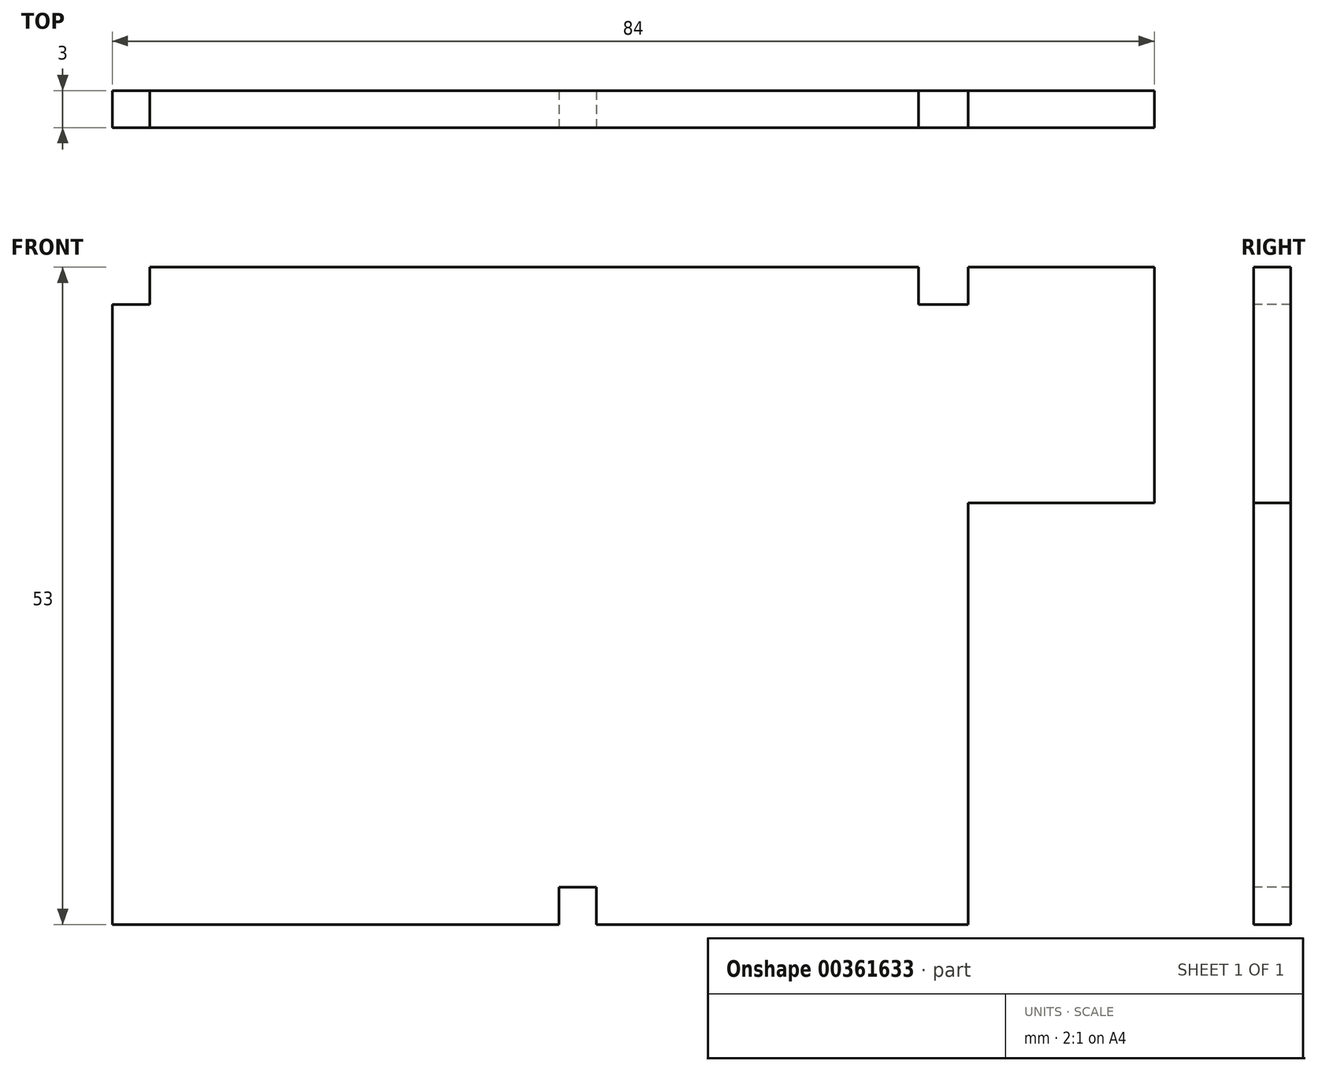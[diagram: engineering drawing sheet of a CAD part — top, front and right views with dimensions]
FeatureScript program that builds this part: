
annotation { "Feature Type Name" : "Feature", "Feature Type Description" : "" }
export const myFeature = defineFeature(function(context is Context, id is Id, definition is map)
    precondition{}
    {
        {
            var Q0;
            Q0=qCreatedBy(makeId("Front.planeOp"),FACE);
            var sketch = newSketch(context, id + "F0", { "sketchPlane" : qUnion([Q0])});
            skLineSegment(sketch, "E0.bottom", {"start": v(-24.73, 20.13) * mm, "end": v(59.27, 20.13) * mm});
            skLineSegment(sketch, "E0.top", {"start": v(-24.73, -32.87) * mm, "end": v(59.27, -32.87) * mm});
            skLineSegment(sketch, "E0.left", {"start": v(-24.73, 20.13) * mm, "end": v(-24.73, -32.87) * mm});
            skLineSegment(sketch, "E0.right", {"start": v(59.27, 20.13) * mm, "end": v(59.27, -32.87) * mm});
            skSolve(sketch);
        }
        {
            var Q0;
            Q0 = qSketchRegion(id + "F0", true);
            extrude(context, id + "F1", {"entities" : qUnion([Q0]), "depth" : 3 * mm});
        }
        {
            var Q0;
            Q0=makeQuery(id+"F1.opExtrude","CAP_FACE",FACE,{"disambiguationData":[OSD([sQuery(id+"F0.wireOp",EDGE,"E0.bottom"),sQuery(id+"F0.wireOp",EDGE,"E0.top"),sQuery(id+"F0.wireOp",EDGE,"E0.left"),sQuery(id+"F0.wireOp",EDGE,"E0.right")])],"isStart":false});
            var sketch = newSketch(context, id + "F2", { "sketchPlane" : qUnion([Q0])});
            skLineSegment(sketch, "E1.bottom", {"start": v(59.27, -32.87) * mm, "end": v(44.27, -32.87) * mm});
            skLineSegment(sketch, "E1.top", {"start": v(59.27, 1.13) * mm, "end": v(44.27, 1.13) * mm});
            skLineSegment(sketch, "E1.left", {"start": v(59.27, -32.87) * mm, "end": v(59.27, 1.13) * mm});
            skLineSegment(sketch, "E1.right", {"start": v(44.27, -32.87) * mm, "end": v(44.27, 1.13) * mm});
            skSolve(sketch);
        }
        {
            var Q0;
            Q0 = qSketchRegion(id + "F2", true);
            extrude(context, id + "F3", {"entities" : qUnion([Q0]), "operationType" : NewBodyOperationType.REMOVE, "oppositeDirection" : true, "depth" : 25 * mm});
        }
        {
            var Q0;
            Q0=makeQuery(id+"F1.opExtrude","CAP_FACE",FACE,{"disambiguationData":[OSD([sQuery(id+"F0.wireOp",EDGE,"E0.bottom"),sQuery(id+"F0.wireOp",EDGE,"E0.top"),sQuery(id+"F0.wireOp",EDGE,"E0.left"),sQuery(id+"F0.wireOp",EDGE,"E0.right")])],"isStart":false});
            var sketch = newSketch(context, id + "F4", { "sketchPlane" : qUnion([Q0])});
            skLineSegment(sketch, "E2", {"start": v(59.27, 20.13) * mm, "end": v(44.27, 20.13) * mm});
            skLineSegment(sketch, "E3", {"start": v(44.27, 20.13) * mm, "end": v(44.27, 17.13) * mm});
            skLineSegment(sketch, "E4", {"start": v(44.27, 17.13) * mm, "end": v(40.27, 17.13) * mm});
            skLineSegment(sketch, "E5", {"start": v(40.27, 17.13) * mm, "end": v(40.27, 20.13) * mm});
            skLineSegment(sketch, "E6", {"start": v(40.27, 20.13) * mm, "end": v(44.27, 20.13) * mm});
            skSolve(sketch);
        }
        {
            var Q0;
            Q0 = qSketchRegion(id + "F4", true);
            extrude(context, id + "F5", {"entities" : qUnion([Q0]), "operationType" : NewBodyOperationType.REMOVE, "oppositeDirection" : true, "depth" : 25 * mm});
        }
        {
            var Q0;
            Q0=makeQuery(id+"F1.opExtrude","CAP_FACE",FACE,{"disambiguationData":[OSD([sQuery(id+"F0.wireOp",EDGE,"E0.bottom"),sQuery(id+"F0.wireOp",EDGE,"E0.top"),sQuery(id+"F0.wireOp",EDGE,"E0.left"),sQuery(id+"F0.wireOp",EDGE,"E0.right")])],"isStart":false});
            var sketch = newSketch(context, id + "F6", { "sketchPlane" : qUnion([Q0])});
            skLineSegment(sketch, "E7", {"start": v(-24.73, 20.13) * mm, "end": v(-21.73, 20.13) * mm});
            skLineSegment(sketch, "E8", {"start": v(-21.73, 20.13) * mm, "end": v(-21.73, 17.13) * mm});
            skLineSegment(sketch, "E9", {"start": v(-21.73, 17.13) * mm, "end": v(-24.73, 17.13) * mm});
            skLineSegment(sketch, "E10", {"start": v(-24.73, 17.13) * mm, "end": v(-24.73, 20.13) * mm});
            skSolve(sketch);
        }
        {
            var Q0;
            Q0 = qSketchRegion(id + "F6", true);
            extrude(context, id + "F7", {"entities" : qUnion([Q0]), "operationType" : NewBodyOperationType.REMOVE, "oppositeDirection" : true, "depth" : 25 * mm});
        }
        {
            var Q0;
            Q0=makeQuery(id+"F1.opExtrude","CAP_FACE",FACE,{"disambiguationData":[OSD([sQuery(id+"F0.wireOp",EDGE,"E0.bottom"),sQuery(id+"F0.wireOp",EDGE,"E0.top"),sQuery(id+"F0.wireOp",EDGE,"E0.left"),sQuery(id+"F0.wireOp",EDGE,"E0.right")])],"isStart":false});
            var sketch = newSketch(context, id + "F8", { "sketchPlane" : qUnion([Q0])});
            skLineSegment(sketch, "E11", {"start": v(44.27, -32.87) * mm, "end": v(14.27, -32.87) * mm});
            skLineSegment(sketch, "E12", {"start": v(14.27, -32.87) * mm, "end": v(14.27, -29.87) * mm});
            skLineSegment(sketch, "E13", {"start": v(14.27, -29.87) * mm, "end": v(11.27, -29.87) * mm});
            skLineSegment(sketch, "E14", {"start": v(11.27, -29.87) * mm, "end": v(11.27, -32.87) * mm});
            skLineSegment(sketch, "E15", {"start": v(11.27, -32.87) * mm, "end": v(14.27, -32.87) * mm});
            skSolve(sketch);
        }
        {
            var Q0;
            Q0 = qSketchRegion(id + "F8", true);
            extrude(context, id + "F9", {"entities" : qUnion([Q0]), "operationType" : NewBodyOperationType.REMOVE, "oppositeDirection" : true, "depth" : 25 * mm});
        }
    });
